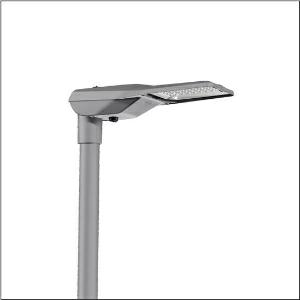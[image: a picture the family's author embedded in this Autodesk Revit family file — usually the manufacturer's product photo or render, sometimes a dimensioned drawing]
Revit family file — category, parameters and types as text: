
# Revit family: streetlight_sl_21_mini___st1_0ab_5xe2m33t08jb_4ee1
name_source: partatom
category: Lighting Fixtures
units: mm (PartAtom-declared; Revit-internal decimal feet)

## family parameters
Cut with Voids When Loaded = No
Host = Face
Light Source = No
Part Type = Normal
Room Calculation Point = No
Round Connector Dimension = Use Diameter
Shared = No

## types (1)
- --- (1 x LED, 11390 lm, 88.6 W, 3000K)
    Apparent Load = 89 VA
    CIE Flux Codes = 40 74 97 100 100
    Color Rendering = 70
    Color Temperature = 3000K
    Default Elevation = 1800 mm
    Description = Streetlight SL 21 mini, mast luminaire, primary light control with lens, of PMMA, primary optical cover: cover, of toughened safety glass, transparent, light distribution: ST1.0aB, light emission: direct distribution, primary light characteristic: asymmetric, installation type: side-entry, post-top, LED, High Power LED, rated luminous flux: 11.390lm, luminous efficacy: 129lm/W, light colour: 730, colour temperature: 3000K, control gear: D4i, control: flexible luminous flux parameterisation, time-dependent luminous flux control, constant luminous flux control, overheat protection, pre-setting: logarithmic dimming characteristic, mains connection: 220..240V, AC, 50/60Hz, start of lifetime: 89W, end of service life: 92W, reduction: 41W, luminaire housing, of diecast aluminium, powder-coated, SITECO metallic grey (DB 702S), corrosivity category C5 high according to DIN EN ISO 12944, please order mast flange separately, inclination adjustable: 0°, 5°, 10°, 15°, sealing non-destructively replaceable, multi-level sealing system, length: 628mm, width: 235mm, height: 110mm, mast flange for spigot size: 42mm (side-entry): 5XC10008XM4, 60/48mm (side-entry/post-top): 5XC10108XM2, 76/60mm (side-entry/post-top): 5XC10108XM1, mounting height: 4..8m, Smart Interface below and above, protection rating (complete): IP66, insulation class (complete): insulation class II (safety insulation), certification: CE, ENEC, ENEC+, VDE, impact resistance: IK10, permissible operating ambient temperature for outdoor applications: -40..+50°C, standard-compliant lighting for roads and squares, packaging unit: 1 piece

Light Distribution: ST1.0aB
    Height = 110 mm
    Lamp = 1 x LED
    Lamp Light Flux = 11390 lm
    Lamp Power = 88.6 W
    Lamp count = 1
    Length = 625 mm
    Luminous efficacy = 129 lm/W
    Manufacturer = Siteco
    ModVariant = No
    Model = 5XE2M33T08JB
    Mounting Place = Pole
    Mounting Type = Pole top
    Number of Poles = 1
    OnlyDefault = Yes
    Power Factor = 1
    Product Name = Streetlight SL 21 mini | ST1.0aB
    Product group = mast luminaire | pylon top
    ProductGroupID = 6100
    Protection Class = Protection class II
    Protection Degree = IP 66
    RLX_Detail_Level = 1
    RLX_Emergency_Light_Flux = 0 lm
    RLX_Emergency_Type = 0
    RLX_Emergency_Type_DB = No
    RlxData = <blob elided: 26389 chars, md5=fd8f034d>
    Socket = socket
    Standby Power = 0 W
    System Light Flux = 11390 lm
    System Power = 89 W
    Type Comments = factory setting: luminous flux: 100 % | dim-lin: 254 | 915 mA
    Type Image = l_1003514.jpg
    URL = http://relux.com
    VarID = @adj_032037
    Voltage = 0 V
    Weight = 0.00 kg
    Width = 234 mm

## geometry (parser evidence)
native form markers: Blend x4, Sweep x9
no freeform markers — native parametric forms only
